# Revit family: Zumtobel SUPERSYSTEM II Track H
name_source: partatom
category: Lighting Fixtures
revit_build: Autodesk Revit 2016 (Build: 20150220_1215(x64)
units: mm (PartAtom-declared; Revit-internal decimal feet)

## family parameters
Cut with Voids When Loaded = No
Host = Face
Light Source = No
OmniClass Number = 23.80.70.11
OmniClass Title = Luminaries for Internal Lighting
Part Type = Normal
Room Calculation Point = No
Round Connector Dimension = Use Diameter
Shared = No

## types (4) — shared parameters
Apparent Load = 0 VA
Assembly Code = D5020200
Emit Shape Visible in Rendering = No
Manufacturer = Zumtobel Lighting
URL = http://www.zumtobel.com
zero-valued in all types: Default Elevation

## per-type parameters (varying)
| type | Description | Length | Model | Track Height | Track Width |
| SUP2 TRACK H 3M | SUP2 Track | 4000 mm  [stored 13.1234 ft] | 22169717 | 60 mm  [stored 0.19685 ft] | 26 mm |
| SUP2 TRACK H 2M | SUP2 Track | 2000 mm  [stored 6.56168 ft] | 22169720 | 60 mm  [stored 0.19685 ft] | 26 mm |
| SUP2 TRACK H 4M | SUP2 Track | 4000 mm  [stored 13.1234 ft] | 22169715 | 60 mm  [stored 0.19685 ft] | 26 mm |
| SUI 3 TRACK H 2M | SUI 3PH/L3+DALI Track | 2000 mm  [stored 6.56168 ft] | S2801260 | 114 mm  [stored 0.374016 ft] | 56 mm  [stored 0.183727 ft] |

note: [stored X ft] marks values corroborated as IEEE doubles in the binary element streams (Revit-internal decimal feet)

## geometry (parser evidence)
native form markers: Sweep x7
no freeform markers — native parametric forms only
